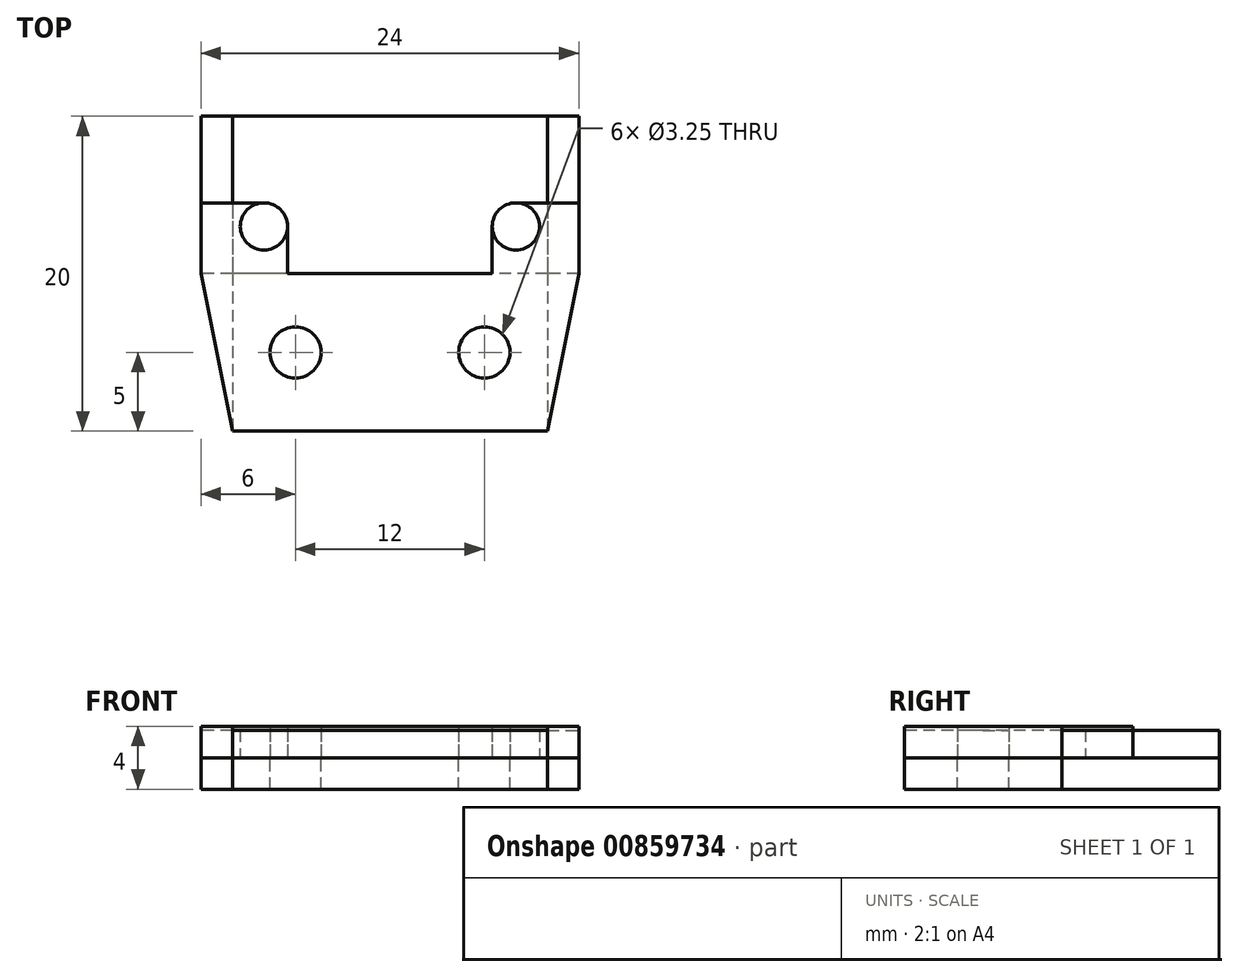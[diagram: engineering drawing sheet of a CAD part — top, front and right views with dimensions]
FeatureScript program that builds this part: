
annotation { "Feature Type Name" : "Feature", "Feature Type Description" : "" }
export const myFeature = defineFeature(function(context is Context, id is Id, definition is map)
    precondition{}
    {
        {
            var Q0;
            Q0=qCreatedBy(makeId("Top.planeOp"),FACE);
            var sketch = newSketch(context, id + "F0", { "sketchPlane" : qUnion([Q0])});
            skLineSegment(sketch, "E0.bottom", {"start": v(-10, 10) * mm, "end": v(10, 10) * mm});
            skLineSegment(sketch, "E0.left", {"start": v(-10, 10) * mm, "end": v(-10, 0) * mm});
            skLineSegment(sketch, "E0.right", {"start": v(10, 10) * mm, "end": v(10, 0) * mm});
            skLineSegment(sketch, "E1.bottom", {"start": v(10, 10) * mm, "end": v(12, 10) * mm});
            skLineSegment(sketch, "E1.right", {"start": v(12, 10) * mm, "end": v(12, 0) * mm});
            skLineSegment(sketch, "E2.bottom", {"start": v(-10, 10) * mm, "end": v(-12, 10) * mm});
            skLineSegment(sketch, "E2.top", {"start": v(-10, 0) * mm, "end": v(-12, 0) * mm});
            skLineSegment(sketch, "E2.right", {"start": v(-12, 10) * mm, "end": v(-12, 0) * mm});
            skCircle(sketch, "E3", {"center": v(-8, 3) * mm, "radius": 1.5 * mm});
            skCircle(sketch, "E4", {"center": v(8, 3) * mm, "radius": 1.5 * mm});
            skLineSegment(sketch, "E5.top", {"start": v(-10, -10) * mm, "end": v(10, -10) * mm});
            skLineSegment(sketch, "E5.left", {"start": v(-10, 0) * mm, "end": v(-10, -10) * mm});
            skLineSegment(sketch, "E5.right", {"start": v(10, 0) * mm, "end": v(10, -10) * mm});
            skPoint(sketch, "E6", {"position": v(-6, -5) * mm});
            skPoint(sketch, "E7", {"position": v(6, -5) * mm});
            skLineSegment(sketch, "E8", {"start": v(10, 0) * mm, "end": v(-10, 0) * mm});
            skLineSegment(sketch, "E9", {"start": v(12, 0) * mm, "end": v(10, 0) * mm});
            skSolve(sketch);
        }
        {
            var Q0;
            Q0=makeQuery(id+"F0.imprint","IMPRINT",FACE,{"disambiguationData":[TD([[makeQuery(id+"F0.imprint","IMPRINT",EDGE,{"derivedFrom":sQuery(id+"F0.wireOp",EDGE,"E5.top")}),1.0]])]});
            extrude(context, id + "F1", {"entities" : qUnion([Q0]), "depth" : 1.75 * mm, "offsetDistance" : 25 * mm});
        }
        {
            var Q0;
            Q0=makeQuery(id+"F0.imprint","IMPRINT",FACE,{"disambiguationData":[TD([[makeQuery(id+"F0.imprint","IMPRINT",EDGE,{"derivedFrom":sQuery(id+"F0.wireOp",EDGE,"E1.bottom")}),-1.0]])]});
            extrude(context, id + "F2", {"entities" : qUnion([Q0]), "depth" : 1.75 * mm, "offsetDistance" : 25 * mm});
        }
        {
            var Q0;
            Q0=makeQuery(id+"F0.imprint","IMPRINT",FACE,{"disambiguationData":[TD([[makeQuery(id+"F0.imprint","IMPRINT",EDGE,{"derivedFrom":sQuery(id+"F0.wireOp",EDGE,"E2.bottom")}),1.0]])]});
            extrude(context, id + "F3", {"entities" : qUnion([Q0]), "depth" : 1.75 * mm, "offsetDistance" : 25 * mm});
        }
        {
            var Q0;
            Q0=makeQuery(id+"F0.imprint","IMPRINT",FACE,{"disambiguationData":[TD([[makeQuery(id+"F0.imprint","IMPRINT",EDGE,{"derivedFrom":sQuery(id+"F0.wireOp",EDGE,"E2.bottom")}),1.0]])]});
            var Q1;
            Q1=makeQuery(id+"F0.imprint","IMPRINT",FACE,{"disambiguationData":[TD([[makeQuery(id+"F0.imprint","IMPRINT",EDGE,{"derivedFrom":sQuery(id+"F0.wireOp",EDGE,"E0.bottom")}),-1.0]])]});
            var Q2;
            Q2=makeQuery(id+"F0.imprint","IMPRINT",FACE,{"disambiguationData":[TD([[makeQuery(id+"F0.imprint","IMPRINT",EDGE,{"derivedFrom":sQuery(id+"F0.wireOp",EDGE,"E3")}),1.0]])]});
            var Q3;
            Q3=makeQuery(id+"F0.imprint","IMPRINT",FACE,{"disambiguationData":[TD([[makeQuery(id+"F0.imprint","IMPRINT",EDGE,{"derivedFrom":sQuery(id+"F0.wireOp",EDGE,"E4")}),1.0]])]});
            var Q4;
            Q4=makeQuery(id+"F0.imprint","IMPRINT",FACE,{"disambiguationData":[TD([[makeQuery(id+"F0.imprint","IMPRINT",EDGE,{"derivedFrom":sQuery(id+"F0.wireOp",EDGE,"E1.bottom")}),-1.0]])]});
            var Q5;
            Q5=makeQuery(id+"F0.imprint","IMPRINT",FACE,{"disambiguationData":[TD([[makeQuery(id+"F0.imprint","IMPRINT",EDGE,{"derivedFrom":sQuery(id+"F0.wireOp",EDGE,"E5.top")}),1.0]])]});
            extrude(context, id + "F4", {"entities" : qUnion([Q0, Q1, Q2, Q3, Q4, Q5]), "oppositeDirection" : true, "depth" : 2 * mm, "offsetDistance" : 25 * mm});
        }
        {
            var Q0;
            Q0=makeQuery(id+"F0.imprint","IMPRINT",FACE,{"disambiguationData":[TD([[makeQuery(id+"F0.imprint","IMPRINT",EDGE,{"derivedFrom":sQuery(id+"F0.wireOp",EDGE,"E3")}),1.0]])]});
            var Q1;
            Q1=makeQuery(id+"F0.imprint","IMPRINT",FACE,{"disambiguationData":[TD([[makeQuery(id+"F0.imprint","IMPRINT",EDGE,{"derivedFrom":sQuery(id+"F0.wireOp",EDGE,"E4")}),1.0]])]});
            extrude(context, id + "F5", {"entities" : qUnion([Q0, Q1]), "operationType" : NewBodyOperationType.ADD, "depth" : 1.75 * mm, "offsetDistance" : 25 * mm});
        }
        {
            var Q0;
            Q0=sQuery(id+"F0.wireOp",VERTEX,"E6");
            var Q1;
            Q1=makeQuery(id+"F1.opExtrude","SWEPT_BODY",BODY,{"disambiguationData":[OSD([sQuery(id+"F0.wireOp",EDGE,"E5.top"),sQuery(id+"F0.wireOp",EDGE,"E5.left"),sQuery(id+"F0.wireOp",EDGE,"E5.right"),sQuery(id+"F0.wireOp",EDGE,"E8")])]});
            hole(context, id + "F6", {"style" : HoleStyle.SIMPLE, "endStyle" : HoleEndStyle.THROUGH, "oppositeDirection" : true, "holeDiameter" : 3.25 * mm, "majorDiameter" : 5 * mm, "isTappedThrough" : true, "tappedDepth" : 12 * mm, "tapClearance" : 3, "locations" : qUnion([Q0]), "scope" : qUnion([Q1])});
        }
        {
            var Q0;
            Q0=sQuery(id+"F0.wireOp",VERTEX,"E7");
            var Q1;
            Q1=makeQuery(id+"F1.opExtrude","SWEPT_BODY",BODY,{"disambiguationData":[OSD([sQuery(id+"F0.wireOp",EDGE,"E5.top"),sQuery(id+"F0.wireOp",EDGE,"E5.left"),sQuery(id+"F0.wireOp",EDGE,"E5.right"),sQuery(id+"F0.wireOp",EDGE,"E8")])]});
            hole(context, id + "F7", {"style" : HoleStyle.SIMPLE, "endStyle" : HoleEndStyle.THROUGH, "oppositeDirection" : true, "holeDiameter" : 3.25 * mm, "majorDiameter" : 5 * mm, "isTappedThrough" : true, "tappedDepth" : 12 * mm, "tapClearance" : 3, "locations" : qUnion([Q0]), "scope" : qUnion([Q1])});
        }
        {
            var Q0;
            Q0=sQuery(id+"F0.wireOp",VERTEX,"E6");
            var Q1;
            Q1=makeQuery(id+"F4.opExtrude","SWEPT_BODY",BODY,{"disambiguationData":[OSD([sQuery(id+"F0.wireOp",EDGE,"E0.bottom"),sQuery(id+"F0.wireOp",EDGE,"E1.bottom"),sQuery(id+"F0.wireOp",EDGE,"E1.right"),sQuery(id+"F0.wireOp",EDGE,"E2.bottom"),sQuery(id+"F0.wireOp",EDGE,"E2.top"),sQuery(id+"F0.wireOp",EDGE,"E2.right"),sQuery(id+"F0.wireOp",EDGE,"E5.top"),sQuery(id+"F0.wireOp",EDGE,"E5.left"),sQuery(id+"F0.wireOp",EDGE,"E5.right"),sQuery(id+"F0.wireOp",EDGE,"E9")])]});
            hole(context, id + "F8", {"style" : HoleStyle.SIMPLE, "endStyle" : HoleEndStyle.THROUGH, "holeDiameter" : 3.25 * mm, "majorDiameter" : 5 * mm, "isTappedThrough" : true, "tappedDepth" : 12 * mm, "tapClearance" : 3, "locations" : qUnion([Q0]), "scope" : qUnion([Q1])});
        }
        {
            var Q0;
            Q0=sQuery(id+"F0.wireOp",VERTEX,"E7");
            var Q1;
            Q1=makeQuery(id+"F4.opExtrude","SWEPT_BODY",BODY,{"disambiguationData":[OSD([sQuery(id+"F0.wireOp",EDGE,"E0.bottom"),sQuery(id+"F0.wireOp",EDGE,"E1.bottom"),sQuery(id+"F0.wireOp",EDGE,"E1.right"),sQuery(id+"F0.wireOp",EDGE,"E2.bottom"),sQuery(id+"F0.wireOp",EDGE,"E2.top"),sQuery(id+"F0.wireOp",EDGE,"E2.right"),sQuery(id+"F0.wireOp",EDGE,"E5.top"),sQuery(id+"F0.wireOp",EDGE,"E5.left"),sQuery(id+"F0.wireOp",EDGE,"E5.right"),sQuery(id+"F0.wireOp",EDGE,"E9")])]});
            hole(context, id + "F9", {"style" : HoleStyle.SIMPLE, "endStyle" : HoleEndStyle.THROUGH, "holeDiameter" : 3.25 * mm, "majorDiameter" : 5 * mm, "isTappedThrough" : true, "tappedDepth" : 12 * mm, "tapClearance" : 3, "locations" : qUnion([Q0]), "scope" : qUnion([Q1])});
        }
        {
            var Q0;
            Q0=qCreatedBy(makeId("Top.planeOp"),FACE);
            var sketch = newSketch(context, id + "F10", { "sketchPlane" : qUnion([Q0])});
            skLineSegment(sketch, "E10", {"start": v(-10, -10) * mm, "end": v(10, -10) * mm});
            skLineSegment(sketch, "E11", {"start": v(10, -10) * mm, "end": v(12, 0) * mm});
            skLineSegment(sketch, "E12", {"start": v(12, 0) * mm, "end": v(12, 4.5) * mm});
            skLineSegment(sketch, "E13", {"start": v(12, 4.5) * mm, "end": v(8, 4.5) * mm});
            skLineSegment(sketch, "E14", {"start": v(6.5, 3) * mm, "end": v(6.5, 0) * mm});
            skLineSegment(sketch, "E15", {"start": v(6.5, 0) * mm, "end": v(-6.5, 0) * mm});
            skLineSegment(sketch, "E16", {"start": v(-6.5, 0) * mm, "end": v(-6.5, 3) * mm});
            skLineSegment(sketch, "E17", {"start": v(-8, 4.5) * mm, "end": v(-12, 4.5) * mm});
            skLineSegment(sketch, "E18", {"start": v(-12, 4.5) * mm, "end": v(-12, 0) * mm});
            skLineSegment(sketch, "E19", {"start": v(-12, 0) * mm, "end": v(-10, -10) * mm});
            skPoint(sketch, "E20.visualSharp", {"position": v(6.5, 4.5) * mm});
            skArc(sketch, "E20.filletArc", {"start": v(8, 4.5) * mm, "mid": v(6.94, 4.06) * mm, "end": v(6.5, 3) * mm});
            skPoint(sketch, "E21.visualSharp", {"position": v(-6.5, 4.5) * mm});
            skArc(sketch, "E21.filletArc", {"start": v(-6.5, 3) * mm, "mid": v(-6.94, 4.06) * mm, "end": v(-8, 4.5) * mm});
            skCircle(sketch, "E22", {"center": v(-6, -5) * mm, "radius": 1.63 * mm});
            skCircle(sketch, "E23", {"center": v(6, -5) * mm, "radius": 1.63 * mm});
            skSolve(sketch);
        }
        {
            var Q0;
            Q0 = qSketchRegion(id + "F10", true);
            extrude(context, id + "F11", {"entities" : qUnion([Q0]), "depth" : 2 * mm, "offsetDistance" : 25 * mm});
        }
    });
